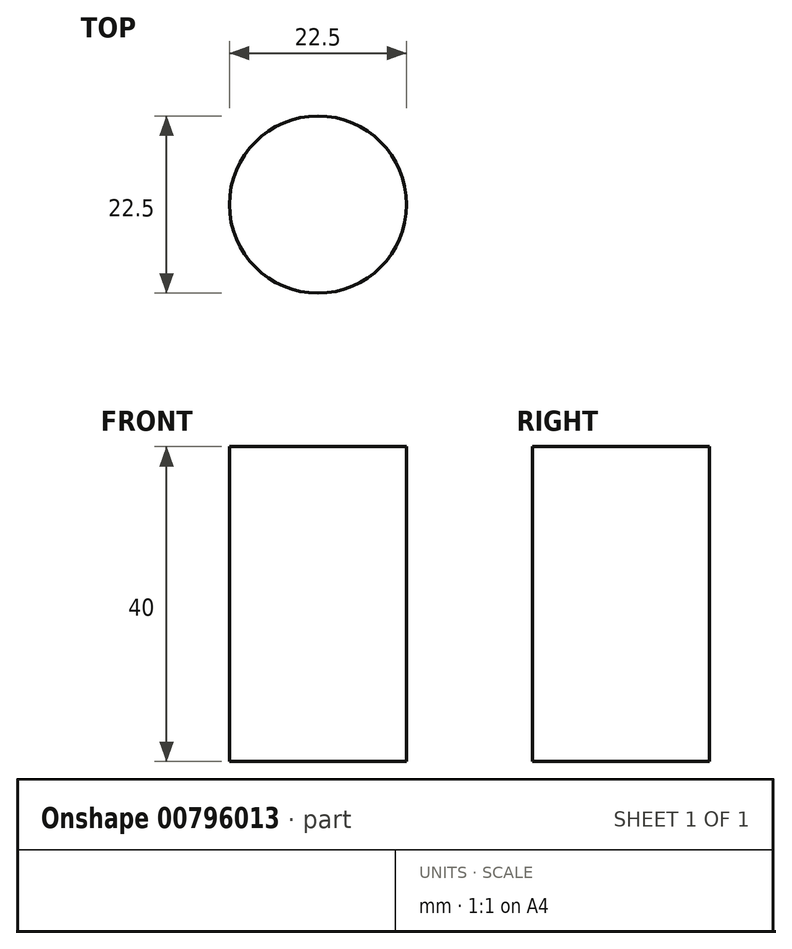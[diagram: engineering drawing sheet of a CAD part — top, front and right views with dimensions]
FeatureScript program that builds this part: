
annotation { "Feature Type Name" : "Feature", "Feature Type Description" : "" }
export const myFeature = defineFeature(function(context is Context, id is Id, definition is map)
    precondition{}
    {
        {
            var Q0;
            Q0=qCreatedBy(makeId("Top.planeOp"),FACE);
            var sketch = newSketch(context, id + "F0", { "sketchPlane" : qUnion([Q0])});
            skCircle(sketch, "E0", {"center": v(0, 0) * mm, "radius": 11.25 * mm});
            skSolve(sketch);
        }
        {
            var Q0;
            Q0 = qSketchRegion(id + "F0", true);
            extrude(context, id + "F1", {"entities" : qUnion([Q0]), "depth" : 40 * mm, "offsetDistance" : 25 * mm});
        }
    });
